# Revit family: Building-IEC309Connections-GEWISS-IEC309HP-10°_FLUSH-MOUNT_SOCKET_16A_REDUCED_FLANGE
name_source: partatom
category: Apparecchi elettrici
units: mm (PartAtom-declared; Revit-internal decimal feet)

## family parameters
Condiviso = No
Host = Superficie
Mantenere orientamento annotazione = Sì
Punto di calcolo locali = Sì
Quota connettore circolare = Usa diametro
Taglio con vuoti quando caricato = No
Tipo di parte = Normale

## types (1)
- GW62204 - IP44 10°P.RECEPTACLE 2P+E 16A 230V 6H
    BLOCCO = B=C
    Breaking capacity at 1.1 Un = 20A
    Catalogue = BUILDING
    Colour: = Blue
    Corpo centrale = Default(2)
    Descrizione = IP44 10°P.RECEPTACLE 2P+E 16A 230V 6H
    Electrocod = 2210
    FORMULA = 1000 mm  [stored 3.28084 ft]
    Flange dimensions (mm) = 62x62
    Frequency = 50/60 Hz
    Glow wire test: = 850 °C (active parts) - 650 °C (passive parts)
    IDF = 0263b613-1a5a-4226-ba06-1b5d4df9bf17
    IDT = 114b7d9d6d3d4d5c9f204bb7cf775f6c
    IP degree = IP44/IP54
    Immagine tipo = <Nessuno>
    Insulation resistance = - 10 M?
    L = 155 mm
    Modello = GW62204
    N.poli = 1
    No. of poles = 2P+E
    Operating temperature: = -25 +55 °C
    Permissible overload = 22A
    Piastra = Default(2)
    Produttore = GEWISS S.p.A.
    Prospetto di default = 1219 mm
    Rated current (A) = 16
    Rated voltage = 200-250V
    Reference h = 6
    SEO = Socket outlet
    SPinotto = Default(2)
    Shock resistance = IK08
    Sportello_visibile = Sì
    Spostamento_S = 963 mm
    Technical sheet = https://www.gewiss.com
    Terminal tightening capacity = 1-2.5mm² flexible cables - 1.5-4mm² rigid cables
    Thermo-pressure with ball = 125 °C (active parts) - 80 °C (passive parts)
    Total number of operations = -5000
    Type of wiring = With screw
    Typology = 10° angled flush-mounting socket-outlet
    URL = https://www.gewiss.com
    Version file RFA = 21.11
    Voltaggio = 0 V
    W = 115 mm

note: [stored X ft] marks values corroborated as IEEE doubles in the binary element streams (Revit-internal decimal feet)

## geometry (parser evidence)
native form markers: Sweep x1
no freeform markers — native parametric forms only
